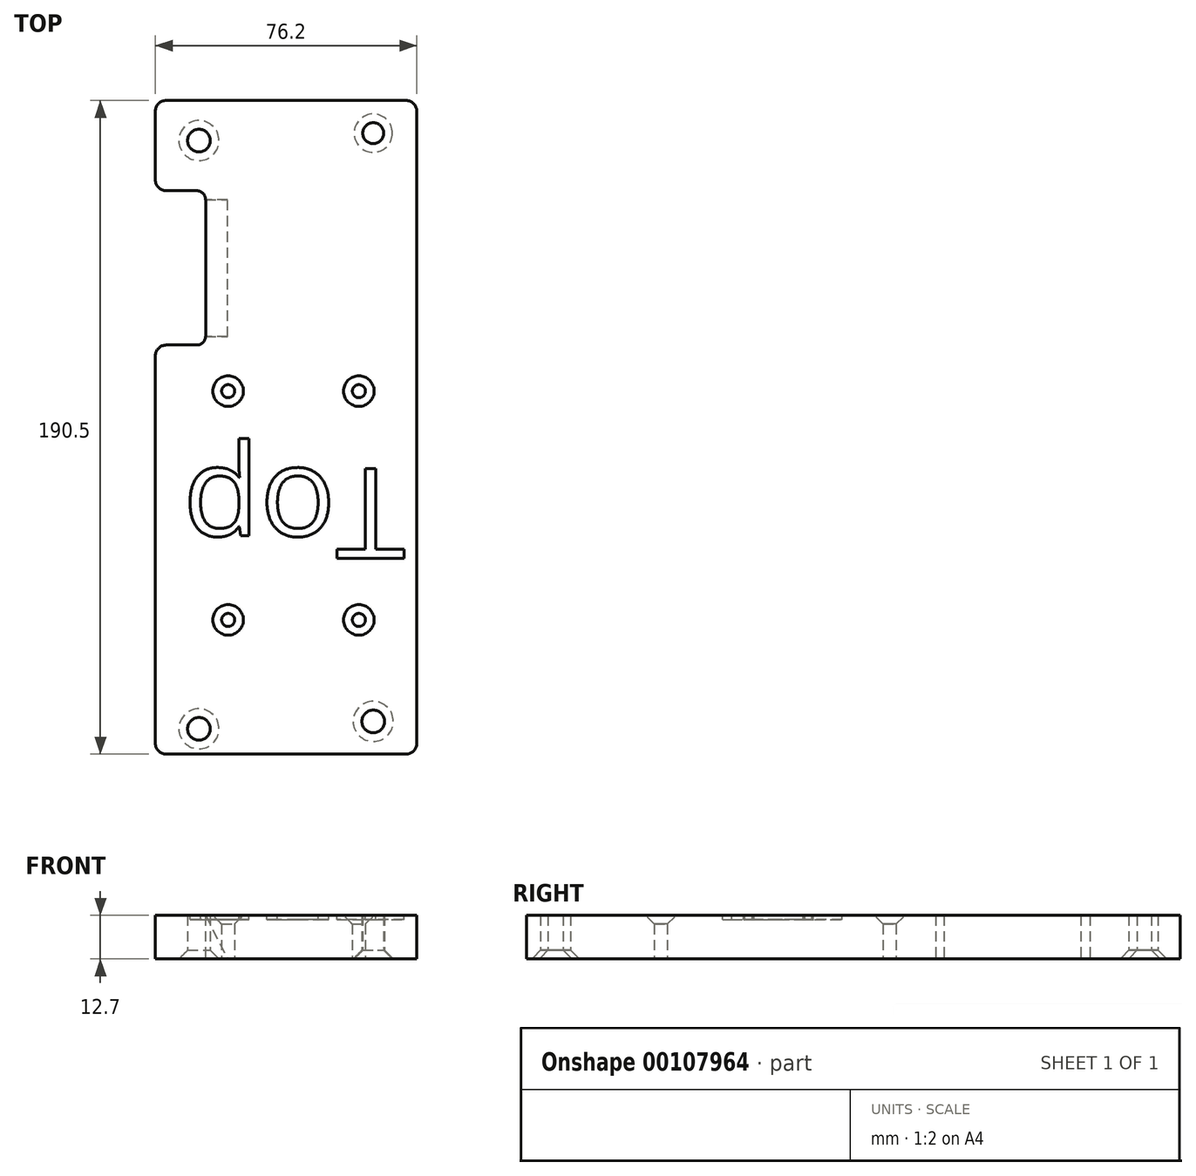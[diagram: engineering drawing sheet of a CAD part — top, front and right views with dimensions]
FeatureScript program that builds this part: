
annotation { "Feature Type Name" : "Feature", "Feature Type Description" : "" }
export const myFeature = defineFeature(function(context is Context, id is Id, definition is map)
    precondition{}
    {
        {
            var Q0;
            Q0=qCreatedBy(makeId("Top.planeOp"),FACE);
            var sketch = newSketch(context, id + "F0", { "sketchPlane" : qUnion([Q0])});
            skLineSegment(sketch, "E0.bottom", {"start": v(40.26, -103.76) * mm, "end": v(-35.94, -103.76) * mm});
            skLineSegment(sketch, "E0.top", {"start": v(40.26, 86.74) * mm, "end": v(-35.94, 86.74) * mm});
            skLineSegment(sketch, "E0.left", {"start": v(40.26, -103.76) * mm, "end": v(40.26, -77.49) * mm});
            skLineSegment(sketch, "E0.right", {"start": v(-35.94, -103.76) * mm, "end": v(-35.94, 86.74) * mm});
            skPoint(sketch, "E0.middle", {"position": v(0, -12.7) * mm});
            skCircle(sketch, "E1", {"center": v(-23.24, -94.23) * mm, "radius": 3.05 * mm});
            skCircle(sketch, "E2", {"center": v(27.56, -92.08) * mm, "radius": 3.3 * mm});
            skCircle(sketch, "E3", {"center": v(-23.24, 77.22) * mm, "radius": 3.3 * mm});
            skCircle(sketch, "E4", {"center": v(27.56, 79.38) * mm, "radius": 3.3 * mm});
            skLineSegment(sketch, "E5", {"start": v(25.65, -35.02) * mm, "end": v(25.65, -74.95) * mm});
            skLineSegment(sketch, "E6.trimOffspring", {"start": v(40.26, -32.48) * mm, "end": v(40.26, 86.74) * mm});
            skLineSegment(sketch, "E7", {"start": v(28.2, -32.48) * mm, "end": v(40.26, -32.48) * mm});
            skLineSegment(sketch, "E8", {"start": v(28.2, -77.49) * mm, "end": v(40.26, -77.49) * mm});
            skCircle(sketch, "E9", {"center": v(-19.05, 47.62) * mm, "radius": 1.9 * mm});
            skCircle(sketch, "E10", {"center": v(19.05, 47.62) * mm, "radius": 1.9 * mm});
            skCircle(sketch, "E11", {"center": v(-19.05, -19.05) * mm, "radius": 1.9 * mm});
            skCircle(sketch, "E12", {"center": v(19.05, -19.05) * mm, "radius": 1.9 * mm});
            skPoint(sketch, "E13.center.orphan", {"position": v(32, -68.98) * mm});
            skPoint(sketch, "E14.center.orphan", {"position": v(32, -38.83) * mm});
            skPoint(sketch, "E15.visualSharp", {"position": v(25.65, -77.49) * mm});
            skArc(sketch, "E15.filletArc", {"start": v(25.65, -74.95) * mm, "mid": v(26.4, -76.74) * mm, "end": v(28.2, -77.49) * mm});
            skPoint(sketch, "E16.visualSharp", {"position": v(25.65, -32.48) * mm});
            skArc(sketch, "E16.filletArc", {"start": v(28.2, -32.48) * mm, "mid": v(26.4, -33.23) * mm, "end": v(25.65, -35.02) * mm});
            skSolve(sketch);
        }
        {
            var Q0;
            Q0=makeQuery(id+"F0.imprint","IMPRINT",FACE,{"disambiguationData":[TD([[makeQuery(id+"F0.imprint","IMPRINT",EDGE,{"derivedFrom":sQuery(id+"F0.wireOp",EDGE,"E0.bottom")}),-1.0]])]});
            extrude(context, id + "F1", {"entities" : qUnion([Q0]), "depth" : 12.7 * mm});
        }
        {
            var Q0;
            Q0=makeQuery(id+"F1.opExtrude","SWEPT_EDGE",EDGE,{"disambiguationData":[OSD([sQuery(id+"F0.wireOp",EDGE,"E0.bottom"),sQuery(id+"F0.wireOp",EDGE,"E0.right")])]});
            var Q1;
            Q1=makeQuery(id+"F1.opExtrude","SWEPT_EDGE",EDGE,{"disambiguationData":[OSD([sQuery(id+"F0.wireOp",EDGE,"E0.bottom"),sQuery(id+"F0.wireOp",EDGE,"E0.left")])]});
            var Q2;
            Q2=makeQuery(id+"F1.opExtrude","SWEPT_EDGE",EDGE,{"disambiguationData":[OSD([sQuery(id+"F0.wireOp",EDGE,"E0.top"),sQuery(id+"F0.wireOp",EDGE,"E6.trimOffspring")])]});
            var Q3;
            Q3=makeQuery(id+"F1.opExtrude","SWEPT_EDGE",EDGE,{"disambiguationData":[OSD([sQuery(id+"F0.wireOp",EDGE,"E0.top"),sQuery(id+"F0.wireOp",EDGE,"E0.right")])]});
            var Q4;
            Q4=makeQuery(id+"F1.opExtrude","SWEPT_EDGE",EDGE,{"disambiguationData":[OSD([sQuery(id+"F0.wireOp",EDGE,"E6.trimOffspring"),sQuery(id+"F0.wireOp",EDGE,"E7")])]});
            var Q5;
            Q5=makeQuery(id+"F1.opExtrude","SWEPT_EDGE",EDGE,{"disambiguationData":[OSD([sQuery(id+"F0.wireOp",EDGE,"E0.left"),sQuery(id+"F0.wireOp",EDGE,"E8")])]});
            fillet(context, id + "F2", {"entities" : qUnion([Q0, Q1, Q2, Q3, Q4, Q5]), "radius" : 3.17 * mm, "tangentPropagation" : true, "allowEdgeOverflow" : false});
        }
        {
            var Q0;
            Q0=makeQuery(id+"F1.opExtrude","CAP_EDGE",EDGE,{"disambiguationData":[OSD([sQuery(id+"F0.wireOp",EDGE,"E12")])],"isStart":false});
            var Q1;
            Q1=makeQuery(id+"F1.opExtrude","CAP_EDGE",EDGE,{"disambiguationData":[OSD([sQuery(id+"F0.wireOp",EDGE,"E11")])],"isStart":false});
            var Q2;
            Q2=makeQuery(id+"F1.opExtrude","CAP_EDGE",EDGE,{"disambiguationData":[OSD([sQuery(id+"F0.wireOp",EDGE,"E9")])],"isStart":false});
            var Q3;
            Q3=makeQuery(id+"F1.opExtrude","CAP_EDGE",EDGE,{"disambiguationData":[OSD([sQuery(id+"F0.wireOp",EDGE,"E10")])],"isStart":false});
            var Q4;
            Q4=makeQuery(id+"F1.opExtrude","CAP_EDGE",EDGE,{"disambiguationData":[OSD([sQuery(id+"F0.wireOp",EDGE,"E4")])],"isStart":true});
            var Q5;
            Q5=makeQuery(id+"F1.opExtrude","CAP_EDGE",EDGE,{"disambiguationData":[OSD([sQuery(id+"F0.wireOp",EDGE,"E3")])],"isStart":true});
            var Q6;
            Q6=makeQuery(id+"F1.opExtrude","CAP_EDGE",EDGE,{"disambiguationData":[OSD([sQuery(id+"F0.wireOp",EDGE,"E2")])],"isStart":true});
            var Q7;
            Q7=makeQuery(id+"F1.opExtrude","CAP_EDGE",EDGE,{"disambiguationData":[OSD([sQuery(id+"F0.wireOp",EDGE,"E1")])],"isStart":true});
            chamfer(context, id + "F3", {"entities" : qUnion([Q0, Q1, Q2, Q3, Q4, Q5, Q6, Q7]), "width" : 2.54 * mm, "tangentPropagation" : true});
        }
        {
            var Q0;
            Q0=makeQuery(id+"F1.opExtrude","CAP_FACE",FACE,{"disambiguationData":[OSD([sQuery(id+"F0.wireOp",EDGE,"E0.bottom"),sQuery(id+"F0.wireOp",EDGE,"E0.top"),sQuery(id+"F0.wireOp",EDGE,"E0.left"),sQuery(id+"F0.wireOp",EDGE,"E0.right"),sQuery(id+"F0.wireOp",EDGE,"E1"),sQuery(id+"F0.wireOp",EDGE,"E2"),sQuery(id+"F0.wireOp",EDGE,"E3"),sQuery(id+"F0.wireOp",EDGE,"E4"),sQuery(id+"F0.wireOp",EDGE,"E14"),sQuery(id+"F0.wireOp",EDGE,"E13"),sQuery(id+"F0.wireOp",EDGE,"E5"),sQuery(id+"F0.wireOp",EDGE,"E6.trimOffspring"),sQuery(id+"F0.wireOp",EDGE,"E7"),sQuery(id+"F0.wireOp",EDGE,"E8"),sQuery(id+"F0.wireOp",EDGE,"E9"),sQuery(id+"F0.wireOp",EDGE,"E10"),sQuery(id+"F0.wireOp",EDGE,"E11"),sQuery(id+"F0.wireOp",EDGE,"E12")])],"isStart":false});
            var sketch = newSketch(context, id + "F4", { "sketchPlane" : qUnion([Q0])});
            skText(sketch, "E17", { "text": "Top", "fontName": "OpenSans-Regular.ttf"});
            const initialGuessF4  = {"E17": [-0.03252, 0.00356, 1, 0, 0.02632]};
            skSetInitialGuess(sketch, initialGuessF4);
            skSolve(sketch);
        }
        {
            var Q0;
            Q0 = qSketchRegion(id + "F4", true);
            extrude(context, id + "F5", {"entities" : qUnion([Q0]), "operationType" : NewBodyOperationType.REMOVE, "oppositeDirection" : true, "depth" : 1.27 * mm});
        }
        {
            var Q0;
            Q0=makeQuery(id+"F1.opExtrude","SWEPT_BODY",BODY,{"disambiguationData":[OSD([sQuery(id+"F0.wireOp",EDGE,"E0.bottom"),sQuery(id+"F0.wireOp",EDGE,"E0.top"),sQuery(id+"F0.wireOp",EDGE,"E0.left"),sQuery(id+"F0.wireOp",EDGE,"E0.right"),sQuery(id+"F0.wireOp",EDGE,"E1"),sQuery(id+"F0.wireOp",EDGE,"E2"),sQuery(id+"F0.wireOp",EDGE,"E3"),sQuery(id+"F0.wireOp",EDGE,"E4"),sQuery(id+"F0.wireOp",EDGE,"E14"),sQuery(id+"F0.wireOp",EDGE,"E13"),sQuery(id+"F0.wireOp",EDGE,"E5"),sQuery(id+"F0.wireOp",EDGE,"E6.trimOffspring"),sQuery(id+"F0.wireOp",EDGE,"E7"),sQuery(id+"F0.wireOp",EDGE,"E8"),sQuery(id+"F0.wireOp",EDGE,"E9"),sQuery(id+"F0.wireOp",EDGE,"E10"),sQuery(id+"F0.wireOp",EDGE,"E11"),sQuery(id+"F0.wireOp",EDGE,"E12")])]});
            var Q1;
            Q1=makeQuery(id+"F1.opExtrude","CAP_EDGE",EDGE,{"disambiguationData":[OSD([sQuery(id+"F0.wireOp",EDGE,"E0.right")])],"isStart":false});
            transform(context, id + "F6", {"entities" : qUnion([Q0]), "transformType" : TransformType.ROTATION, "transformAxis" : qUnion([Q1]), "angle" : 180 * degree, "makeCopy" : false});
        }
        {
            var Q0;
            Q0=makeQuery(id+"F1.opExtrude","SWEPT_BODY",BODY,{"disambiguationData":[OSD([sQuery(id+"F0.wireOp",EDGE,"E0.bottom"),sQuery(id+"F0.wireOp",EDGE,"E0.top"),sQuery(id+"F0.wireOp",EDGE,"E0.left"),sQuery(id+"F0.wireOp",EDGE,"E0.right"),sQuery(id+"F0.wireOp",EDGE,"E1"),sQuery(id+"F0.wireOp",EDGE,"E2"),sQuery(id+"F0.wireOp",EDGE,"E3"),sQuery(id+"F0.wireOp",EDGE,"E4"),sQuery(id+"F0.wireOp",EDGE,"E14"),sQuery(id+"F0.wireOp",EDGE,"E13"),sQuery(id+"F0.wireOp",EDGE,"E5"),sQuery(id+"F0.wireOp",EDGE,"E6.trimOffspring"),sQuery(id+"F0.wireOp",EDGE,"E7"),sQuery(id+"F0.wireOp",EDGE,"E8"),sQuery(id+"F0.wireOp",EDGE,"E9"),sQuery(id+"F0.wireOp",EDGE,"E10"),sQuery(id+"F0.wireOp",EDGE,"E11"),sQuery(id+"F0.wireOp",EDGE,"E12")])]});
            var Q1;
            Q1=makeQuery(id+"F1.opExtrude","CAP_EDGE",EDGE,{"disambiguationData":[OSD([sQuery(id+"F0.wireOp",EDGE,"E0.bottom")])],"isStart":true});
            var Q2;
            Q2=makeQuery(id+"F1.opExtrude","CAP_EDGE",EDGE,{"disambiguationData":[OSD([sQuery(id+"F0.wireOp",EDGE,"E0.bottom")])],"isStart":true});
            transform(context, id + "F7", {"entities" : qUnion([Q0]), "transformType" : TransformType.ROTATION, "transformAxis" : qUnion([Q2]), "angle" : 180 * degree, "makeCopy" : false});
        }
        {
            var Q0;
            Q0=makeQuery(id+"F1.opExtrude","SWEPT_FACE",FACE,{"disambiguationData":[OSD([sQuery(id+"F0.wireOp",EDGE,"E0.bottom")])]});
            cPlane(context, id + "F8", {"entities" : qUnion([Q0]), "cplaneType" : CPlaneType.OFFSET, "offset" : 28.96 * mm, "oppositeDirection" : true, "width" : 152.4 * mm, "height" : 152.4 * mm});
        }
        {
            var Q0;
            Q0=qCreatedBy(id+"F8.planeOp",FACE);
            var sketch = newSketch(context, id + "F9", { "sketchPlane" : qUnion([Q0])});
            skLineSegment(sketch, "E18", {"start": v(98.34, 39.76) * mm, "end": v(90.27, 23.76) * mm});
            skLineSegment(sketch, "E19", {"start": v(98.34, 39.76) * mm, "end": v(98.34, 23.76) * mm});
            skLineSegment(sketch, "E20", {"start": v(98.34, 23.76) * mm, "end": v(90.27, 23.76) * mm});
            skSolve(sketch);
        }
        {
            var Q0;
            Q0=makeQuery(id+"F9.imprint","IMPRINT",FACE,{"disambiguationData":[TD([[makeQuery(id+"F9.imprint","IMPRINT",EDGE,{"derivedFrom":sQuery(id+"F9.wireOp",EDGE,"E18")}),1.0]])]});
            extrude(context, id + "F10", {"entities" : qUnion([Q0]), "operationType" : NewBodyOperationType.REMOVE, "oppositeDirection" : true, "depth" : 39.88 * mm});
        }
        {
            var Q0;
            Q0=makeQuery(id+"F1.opExtrude","SWEPT_BODY",BODY,{"disambiguationData":[OSD([sQuery(id+"F0.wireOp",EDGE,"E0.bottom"),sQuery(id+"F0.wireOp",EDGE,"E0.top"),sQuery(id+"F0.wireOp",EDGE,"E0.left"),sQuery(id+"F0.wireOp",EDGE,"E0.right"),sQuery(id+"F0.wireOp",EDGE,"E1"),sQuery(id+"F0.wireOp",EDGE,"E2"),sQuery(id+"F0.wireOp",EDGE,"E3"),sQuery(id+"F0.wireOp",EDGE,"E4"),sQuery(id+"F0.wireOp",EDGE,"E5"),sQuery(id+"F0.wireOp",EDGE,"E6.trimOffspring"),sQuery(id+"F0.wireOp",EDGE,"E7"),sQuery(id+"F0.wireOp",EDGE,"E8"),sQuery(id+"F0.wireOp",EDGE,"E9"),sQuery(id+"F0.wireOp",EDGE,"E10"),sQuery(id+"F0.wireOp",EDGE,"E11"),sQuery(id+"F0.wireOp",EDGE,"E12"),sQuery(id+"F0.wireOp",EDGE,"E15.filletArc"),sQuery(id+"F0.wireOp",EDGE,"E16.filletArc")])]});
            transform(context, id + "F11", {"entities" : qUnion([Q0]), "transformType" : TransformType.TRANSLATION_3D, "dx" : 71.12 * mm, "dy" : 190.5 * mm, "dz" : 0 * mm, "makeCopy" : false});
        }
    });
